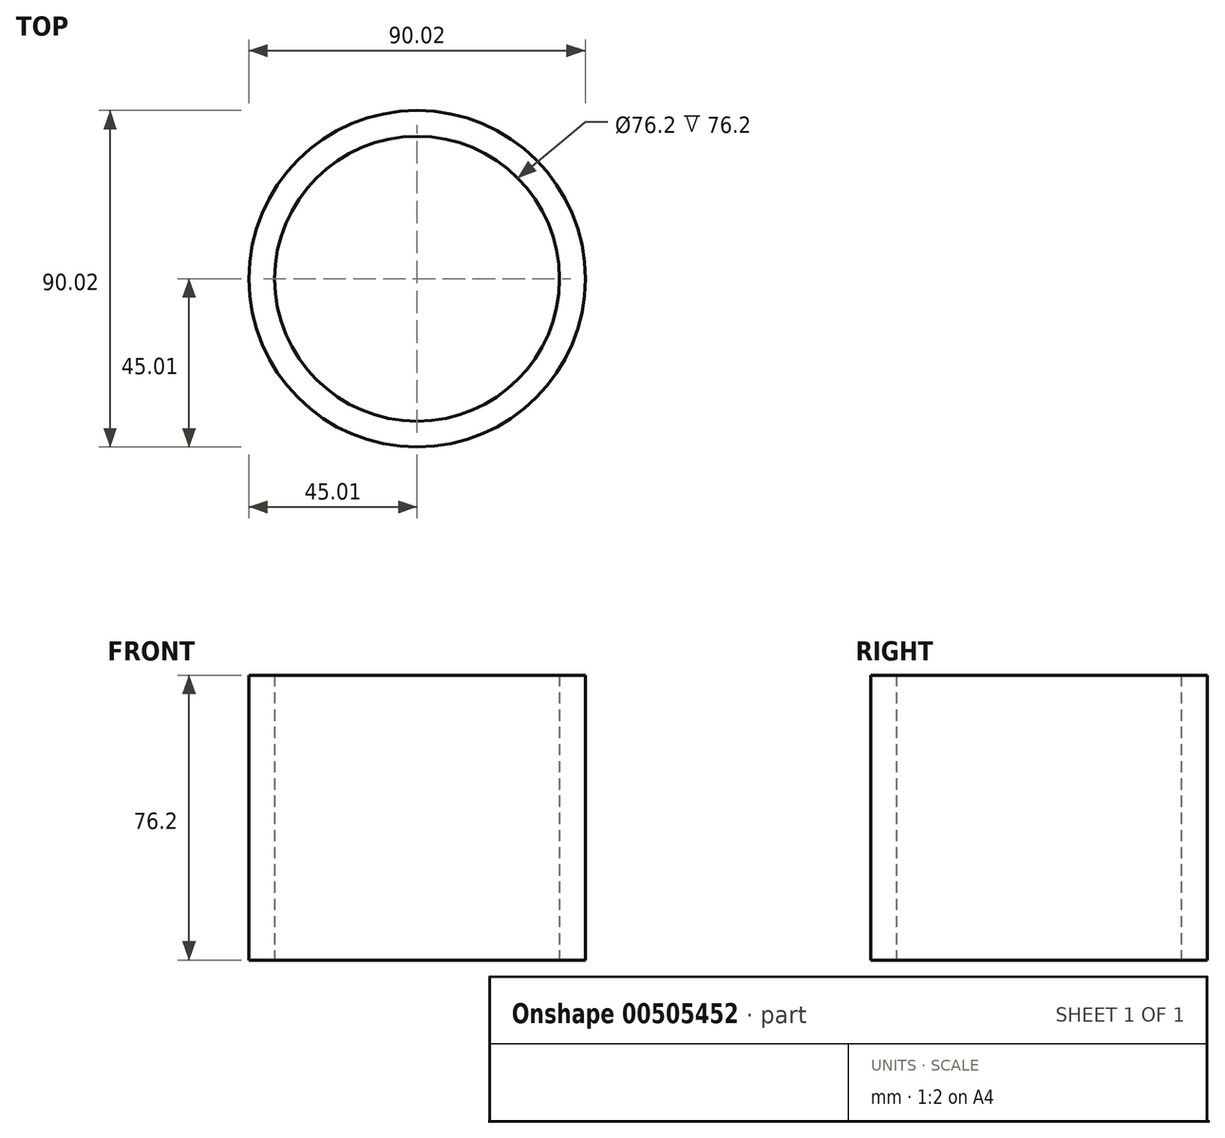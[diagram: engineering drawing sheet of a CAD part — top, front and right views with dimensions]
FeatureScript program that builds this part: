
annotation { "Feature Type Name" : "Feature", "Feature Type Description" : "" }
export const myFeature = defineFeature(function(context is Context, id is Id, definition is map)
    precondition{}
    {
        {
            var Q0;
            Q0=qCreatedBy(makeId("Top.planeOp"),FACE);
            var sketch = newSketch(context, id + "F0", { "sketchPlane" : qUnion([Q0])});
            skCircle(sketch, "E0", {"center": v(0, 0) * mm, "radius": 38.1 * mm});
            skCircle(sketch, "E1", {"center": v(0, 0) * mm, "radius": 45.01 * mm});
            skSolve(sketch);
        }
        {
            var Q0;
            Q0 = qSketchRegion(id + "F0", true);
            extrude(context, id + "F1", {"entities" : qUnion([Q0]), "depth" : 76.2 * mm});
        }
    });
